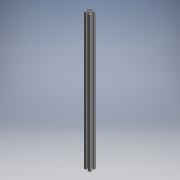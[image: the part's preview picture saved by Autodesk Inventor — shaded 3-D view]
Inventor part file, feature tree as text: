
AUTODESK INVENTOR PART (.ipt)
format: ipt  version: 2017.3 (Build 213256000, 256)  size: 207,872 bytes
history: native  units: mm (DEFAULTED — no unit token found)
features: other x7, sketch x2, extrude x1, hole x1
ambient origin geometry x8: Origin, YZ Plane, XZ Plane, XY Plane, X Axis, Y Axis, Z Axis, Center Point
bodies: Solid1 (feature_tree)
feature tree (11):
  extrude  "Extrusion1"  TaperAngle=0.0deg  [1 undecoded]
  hole  "Hole1"  [1 undecoded]
  other  "C1_XY"
  other  "C1_YZ"
  other  "C1_ZX"
  other  "C1_X"
  other  "C1_Y"
  other  "C1_Z"
  other  "C1_Center"
  sketch  "Sketch_75"  dims[d2=4.2mm d3=6.0mm d4=4.0mm d5=2.0mm d6=90.0deg d7=437.0mm d8=0.0mm d9=0.0mm]
  sketch  "Sketch2"  dims[d0=437.0mm d1=0.0mm]
note: 2 required parameter values undecoded (feature->parameter linkage not recoverable at this tier; creation-order binding heuristic only, values carry confidence <= 0.55)
